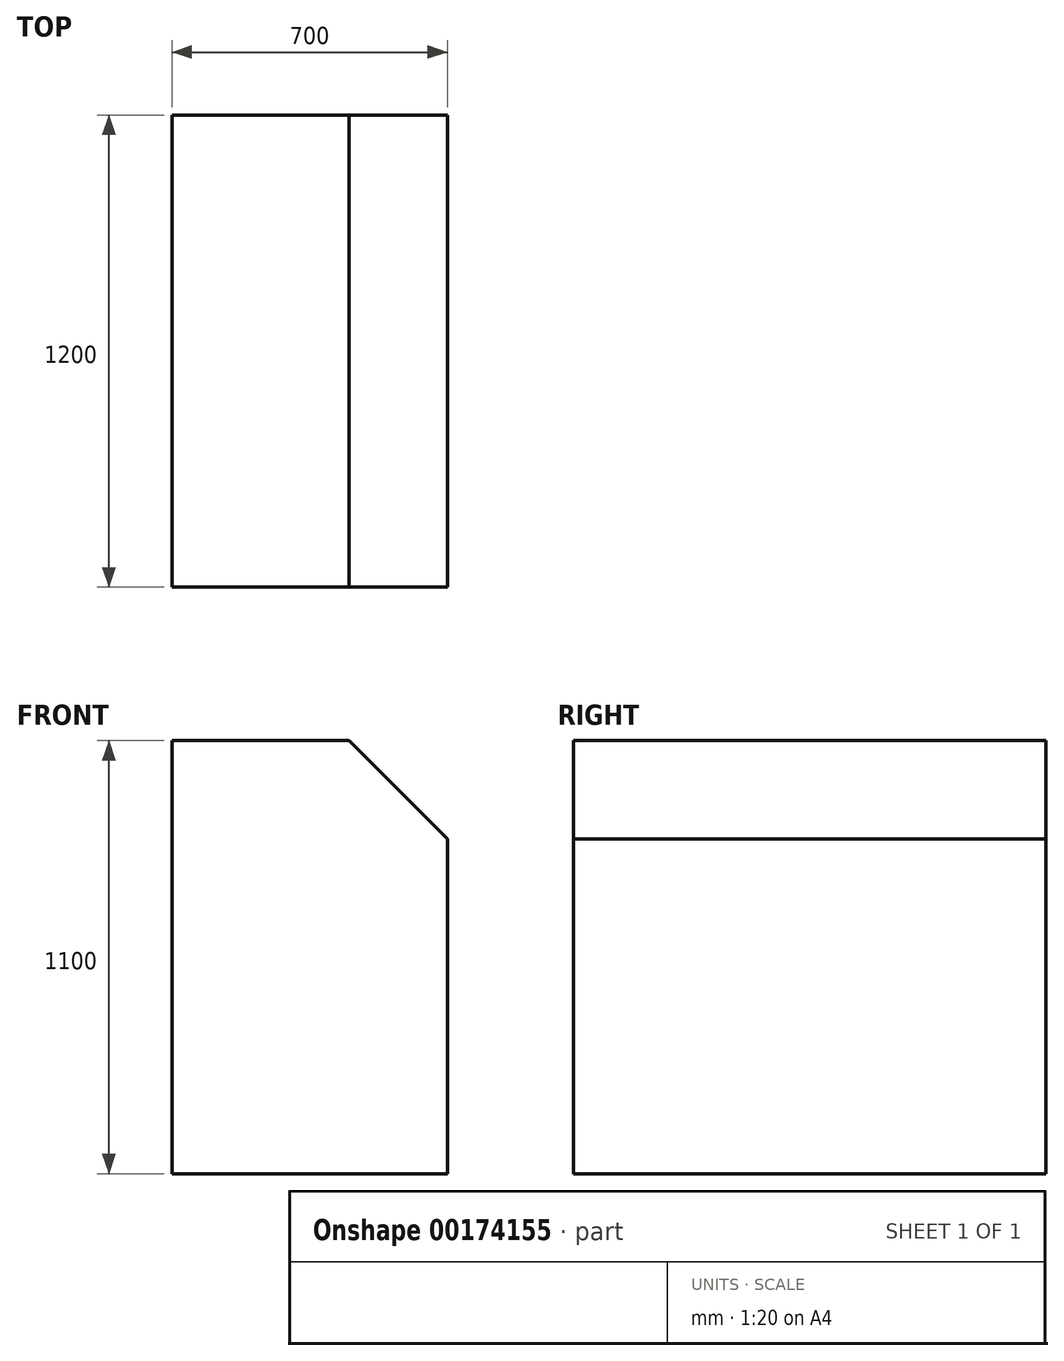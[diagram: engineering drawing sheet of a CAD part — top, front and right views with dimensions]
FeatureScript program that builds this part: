
annotation { "Feature Type Name" : "Feature", "Feature Type Description" : "" }
export const myFeature = defineFeature(function(context is Context, id is Id, definition is map)
    precondition{}
    {
        {
            var Q0;
            Q0=qCreatedBy(makeId("Top.planeOp"),FACE);
            var sketch = newSketch(context, id + "F0", { "sketchPlane" : qUnion([Q0])});
            skLineSegment(sketch, "E0.bottom", {"start": v(0, 0) * mm, "end": v(700, 0) * mm});
            skLineSegment(sketch, "E0.top", {"start": v(0, 1200) * mm, "end": v(700, 1200) * mm});
            skLineSegment(sketch, "E0.left", {"start": v(0, 0) * mm, "end": v(0, 1200) * mm});
            skLineSegment(sketch, "E0.right", {"start": v(700, 0) * mm, "end": v(700, 1200) * mm});
            skSolve(sketch);
        }
        {
            var Q0;
            Q0=makeQuery(id+"F0.imprint","IMPRINT",FACE,{"disambiguationData":[TD([[makeQuery(id+"F0.imprint","IMPRINT",EDGE,{"derivedFrom":sQuery(id+"F0.wireOp",EDGE,"E0.bottom")}),1.0]])]});
            extrude(context, id + "F1", {"entities" : qUnion([Q0]), "depth" : 1100 * mm});
        }
        {
            var Q0;
            Q0=makeQuery(id+"F1.opExtrude","CAP_EDGE",EDGE,{"disambiguationData":[OSD([sQuery(id+"F0.wireOp",EDGE,"E0.right")])],"isStart":false});
            chamfer(context, id + "F2", {"entities" : qUnion([Q0]), "width" : 250 * mm, "tangentPropagation" : true});
        }
    });
